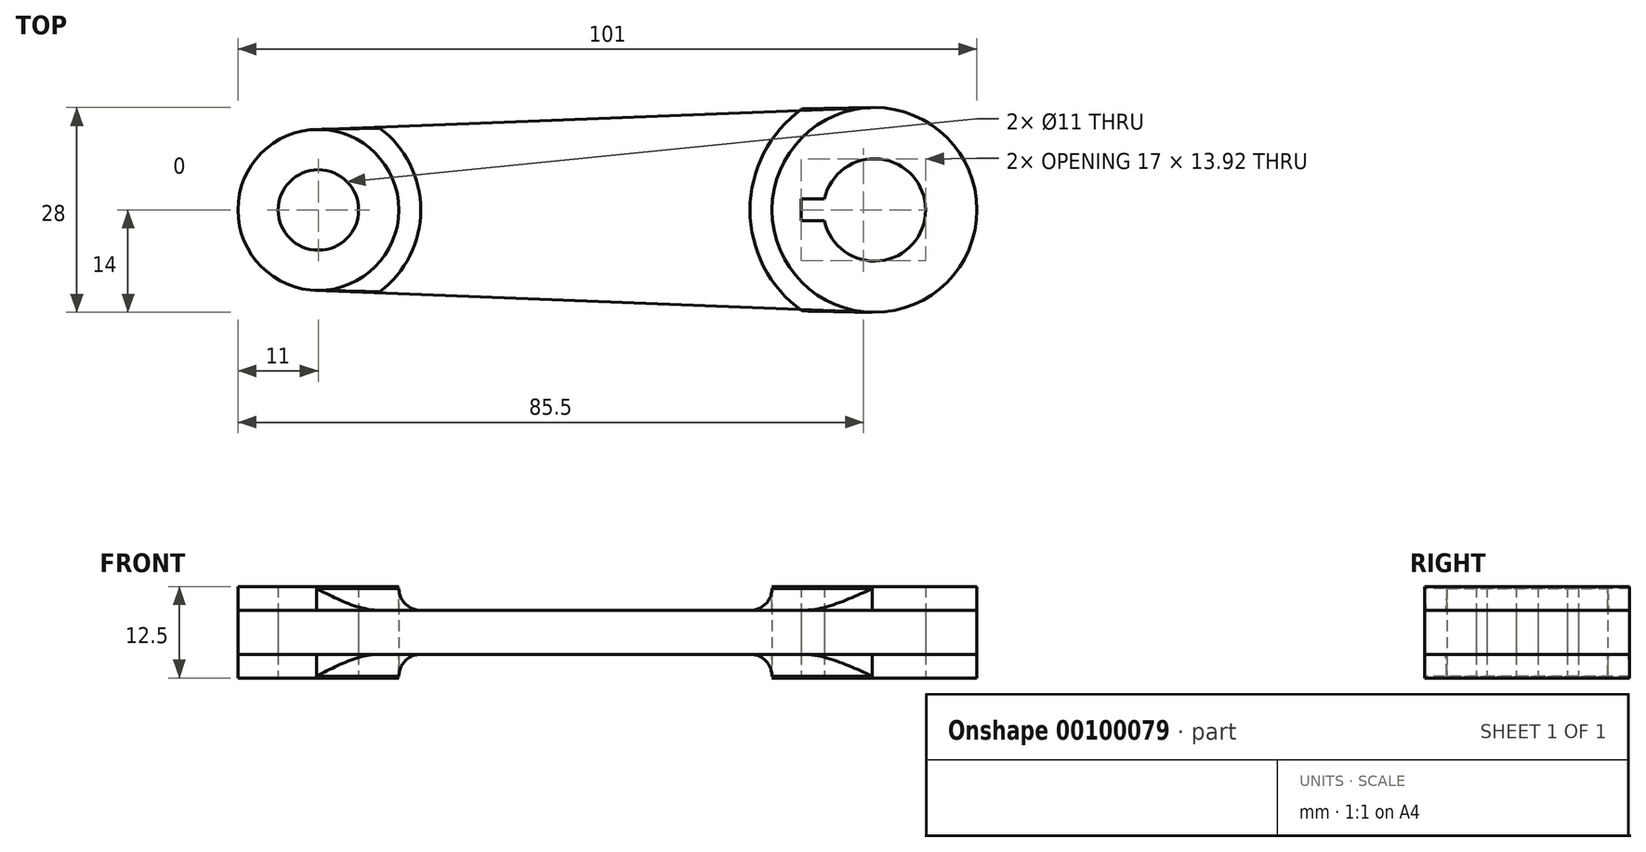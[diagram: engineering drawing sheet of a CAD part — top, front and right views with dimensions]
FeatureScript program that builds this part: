
annotation { "Feature Type Name" : "Feature", "Feature Type Description" : "" }
export const myFeature = defineFeature(function(context is Context, id is Id, definition is map)
    precondition{}
    {
        {
            var Q0;
            Q0=qCreatedBy(makeId("Top.planeOp"),FACE);
            var sketch = newSketch(context, id + "F0", { "sketchPlane" : qUnion([Q0])});
            skArc(sketch, "E0", {"start": v(-6.84, -1.5) * mm, "mid": v(7, 0) * mm, "end": v(-6.84, 1.5) * mm});
            skCircle(sketch, "E1", {"center": v(0, 0) * mm, "radius": 14 * mm});
            skCircle(sketch, "E2", {"center": v(-76, 0) * mm, "radius": 5.5 * mm});
            skCircle(sketch, "E3", {"center": v(-76, 0) * mm, "radius": 11 * mm});
            skLineSegment(sketch, "E4", {"start": v(-76.43, 11) * mm, "end": v(0, 14.01) * mm});
            skLineSegment(sketch, "E5", {"start": v(-76.43, -11) * mm, "end": v(-0.55, -13.99) * mm});
            skLineSegment(sketch, "E6", {"start": v(-10, 1.5) * mm, "end": v(-10, -1.5) * mm});
            skLineSegment(sketch, "E7", {"start": v(-10, 1.5) * mm, "end": v(-6.84, 1.5) * mm});
            skLineSegment(sketch, "E8", {"start": v(-10, -1.5) * mm, "end": v(-6.84, -1.5) * mm});
            skLineSegment(sketch, "E9", {"start": v(-76.43, -11) * mm, "end": v(0, -11) * mm, "construction": true});
            skSolve(sketch);
        }
        {
            var Q0;
            Q0=makeQuery(id+"F0.imprint","IMPRINT",FACE,{"disambiguationData":[TD([[makeQuery(id+"F0.imprint","IMPRINT",EDGE,{"derivedFrom":sQuery(id+"F0.wireOp",EDGE,"E2")}),-1.0]])]});
            var Q1;
            Q1=makeQuery(id+"F0.imprint","IMPRINT",FACE,{"disambiguationData":[TD([[makeQuery(id+"F0.imprint","IMPRINT",EDGE,{"derivedFrom":sQuery(id+"F0.wireOp",EDGE,"E0")}),-1.0]])]});
            extrude(context, id + "F1", {"entities" : qUnion([Q0, Q1]), "endBound" : BoundingType.SYMMETRIC, "depth" : 12.5 * mm});
        }
        {
            var Q0;
            Q0 = qSketchRegion(id + "F0", true);
            extrude(context, id + "F2", {"entities" : qUnion([Q0]), "endBound" : BoundingType.SYMMETRIC, "depth" : 6 * mm});
        }
        {
            var Q0;
            Q0=qCreatedBy(makeId("Front.planeOp"),FACE);
            var sketch = newSketch(context, id + "F3", { "sketchPlane" : qUnion([Q0])});
            skArc(sketch, "E10", {"start": v(-65, 6) * mm, "mid": v(-64.12, 3.88) * mm, "end": v(-62, 3) * mm});
            skLineSegment(sketch, "E11", {"start": v(-65, 3) * mm, "end": v(-65, 9.2) * mm, "construction": true});
            skLineSegment(sketch, "E12", {"start": v(-65, 3) * mm, "end": v(-52.33, 3) * mm, "construction": true});
            skLineSegment(sketch, "E13", {"start": v(-65, 6) * mm, "end": v(-65, 3) * mm});
            skLineSegment(sketch, "E14", {"start": v(-62, 3) * mm, "end": v(-65, 3) * mm});
            skLineSegment(sketch, "E15", {"start": v(-76, 24.5) * mm, "end": v(-76, -22.06) * mm, "construction": true});
            skLineSegment(sketch, "E16.MirrorCS", {"start": v(-62, -3) * mm, "end": v(-65, -3) * mm});
            skLineSegment(sketch, "E17.MirrorCS", {"start": v(-65, -6) * mm, "end": v(-65, -3) * mm});
            skArc(sketch, "E18.MirrorCS", {"start": v(-65, -6) * mm, "mid": v(-64.12, -3.88) * mm, "end": v(-62, -3) * mm});
            skLineSegment(sketch, "E19", {"start": v(-14, 3) * mm, "end": v(-14, 6) * mm});
            skLineSegment(sketch, "E20", {"start": v(-14, 3) * mm, "end": v(-17, 3) * mm});
            skArc(sketch, "E21", {"start": v(-14, 6) * mm, "mid": v(-14.88, 3.88) * mm, "end": v(-17, 3) * mm});
            skLineSegment(sketch, "E22.MirrorCS", {"start": v(-14, -3) * mm, "end": v(-14, -6) * mm});
            skLineSegment(sketch, "E23.MirrorCS", {"start": v(-14, -3) * mm, "end": v(-17, -3) * mm});
            skArc(sketch, "E24.MirrorCS", {"start": v(-14, -6) * mm, "mid": v(-14.88, -3.88) * mm, "end": v(-17, -3) * mm});
            skLineSegment(sketch, "E25", {"start": v(0, 40.72) * mm, "end": v(0, -63.9) * mm, "construction": true});
            skSolve(sketch);
        }
        {
            var Q0;
            Q0=makeQuery(id+"F3.imprint","IMPRINT",FACE,{"disambiguationData":[TD([[makeQuery(id+"F3.imprint","IMPRINT",EDGE,{"derivedFrom":sQuery(id+"F3.wireOp",EDGE,"E10")}),-1.0]])]});
            var Q1;
            Q1=makeQuery(id+"F3.imprint","IMPRINT",FACE,{"disambiguationData":[TD([[makeQuery(id+"F3.imprint","IMPRINT",EDGE,{"derivedFrom":sQuery(id+"F3.wireOp",EDGE,"E16.MirrorCS")}),1.0]])]});
            var Q2;
            Q2=sQuery(id+"F3.wireOp",EDGE,"E15");
            revolve(context, id + "F4", {"entities" : qUnion([Q0, Q1]), "axis" : qUnion([Q2]), "revolveType" : RevolveType.SYMMETRIC, "angle" : 182.62 * degree});
        }
        {
            var Q0;
            Q0=makeQuery(id+"F3.imprint","IMPRINT",FACE,{"disambiguationData":[TD([[makeQuery(id+"F3.imprint","IMPRINT",EDGE,{"derivedFrom":sQuery(id+"F3.wireOp",EDGE,"E19")}),1.0]])]});
            var Q1;
            Q1=makeQuery(id+"F3.imprint","IMPRINT",FACE,{"disambiguationData":[TD([[makeQuery(id+"F3.imprint","IMPRINT",EDGE,{"derivedFrom":sQuery(id+"F3.wireOp",EDGE,"E22.MirrorCS")}),-1.0]])]});
            var Q2;
            Q2=sQuery(id+"F3.wireOp",EDGE,"E25");
            revolve(context, id + "F5", {"entities" : qUnion([Q0, Q1]), "axis" : qUnion([Q2]), "revolveType" : RevolveType.SYMMETRIC, "angle" : 177.74 * degree});
        }
        {
            var Q0;
            Q0=makeQuery(id+"F4.opRevolve","CAP_FACE",FACE,{"disambiguationData":[OSD([sQuery(id+"F3.wireOp",EDGE,"E10"),sQuery(id+"F3.wireOp",EDGE,"E13"),sQuery(id+"F3.wireOp",EDGE,"E14")])],"isStart":false});
            var Q1;
            Q1=makeQuery(id+"F4.opRevolve","CAP_FACE",FACE,{"disambiguationData":[OSD([sQuery(id+"F3.wireOp",EDGE,"E16.MirrorCS"),sQuery(id+"F3.wireOp",EDGE,"E17.MirrorCS"),sQuery(id+"F3.wireOp",EDGE,"E18.MirrorCS")])],"isStart":false});
            extrude(context, id + "F6", {"entities" : qUnion([Q0, Q1]), "operationType" : NewBodyOperationType.REMOVE, "oppositeDirection" : true, "depth" : 25 * mm});
        }
        {
            var Q0;
            Q0=makeQuery(id+"F4.opRevolve","CAP_FACE",FACE,{"disambiguationData":[OSD([sQuery(id+"F3.wireOp",EDGE,"E10"),sQuery(id+"F3.wireOp",EDGE,"E13"),sQuery(id+"F3.wireOp",EDGE,"E14")])],"isStart":true});
            var Q1;
            Q1=makeQuery(id+"F4.opRevolve","CAP_FACE",FACE,{"disambiguationData":[OSD([sQuery(id+"F3.wireOp",EDGE,"E16.MirrorCS"),sQuery(id+"F3.wireOp",EDGE,"E17.MirrorCS"),sQuery(id+"F3.wireOp",EDGE,"E18.MirrorCS")])],"isStart":true});
            extrude(context, id + "F7", {"entities" : qUnion([Q0, Q1]), "operationType" : NewBodyOperationType.REMOVE, "oppositeDirection" : true, "depth" : 25 * mm});
        }
        {
            var Q0;
            Q0=makeQuery(id+"F5.opRevolve","CAP_FACE",FACE,{"disambiguationData":[OSD([sQuery(id+"F3.wireOp",EDGE,"E19"),sQuery(id+"F3.wireOp",EDGE,"E20"),sQuery(id+"F3.wireOp",EDGE,"E21")])],"isStart":true});
            var Q1;
            Q1=makeQuery(id+"F5.opRevolve","CAP_FACE",FACE,{"disambiguationData":[OSD([sQuery(id+"F3.wireOp",EDGE,"E22.MirrorCS"),sQuery(id+"F3.wireOp",EDGE,"E23.MirrorCS"),sQuery(id+"F3.wireOp",EDGE,"E24.MirrorCS")])],"isStart":true});
            extrude(context, id + "F8", {"entities" : qUnion([Q0, Q1]), "operationType" : NewBodyOperationType.REMOVE, "oppositeDirection" : true, "depth" : 25 * mm});
        }
        {
            var Q0;
            Q0=makeQuery(id+"F5.opRevolve","CAP_FACE",FACE,{"disambiguationData":[OSD([sQuery(id+"F3.wireOp",EDGE,"E22.MirrorCS"),sQuery(id+"F3.wireOp",EDGE,"E23.MirrorCS"),sQuery(id+"F3.wireOp",EDGE,"E24.MirrorCS")])],"isStart":false});
            var Q1;
            Q1=makeQuery(id+"F5.opRevolve","CAP_FACE",FACE,{"disambiguationData":[OSD([sQuery(id+"F3.wireOp",EDGE,"E19"),sQuery(id+"F3.wireOp",EDGE,"E20"),sQuery(id+"F3.wireOp",EDGE,"E21")])],"isStart":false});
            extrude(context, id + "F9", {"entities" : qUnion([Q0, Q1]), "operationType" : NewBodyOperationType.REMOVE, "oppositeDirection" : true, "depth" : 25 * mm});
        }
    });
